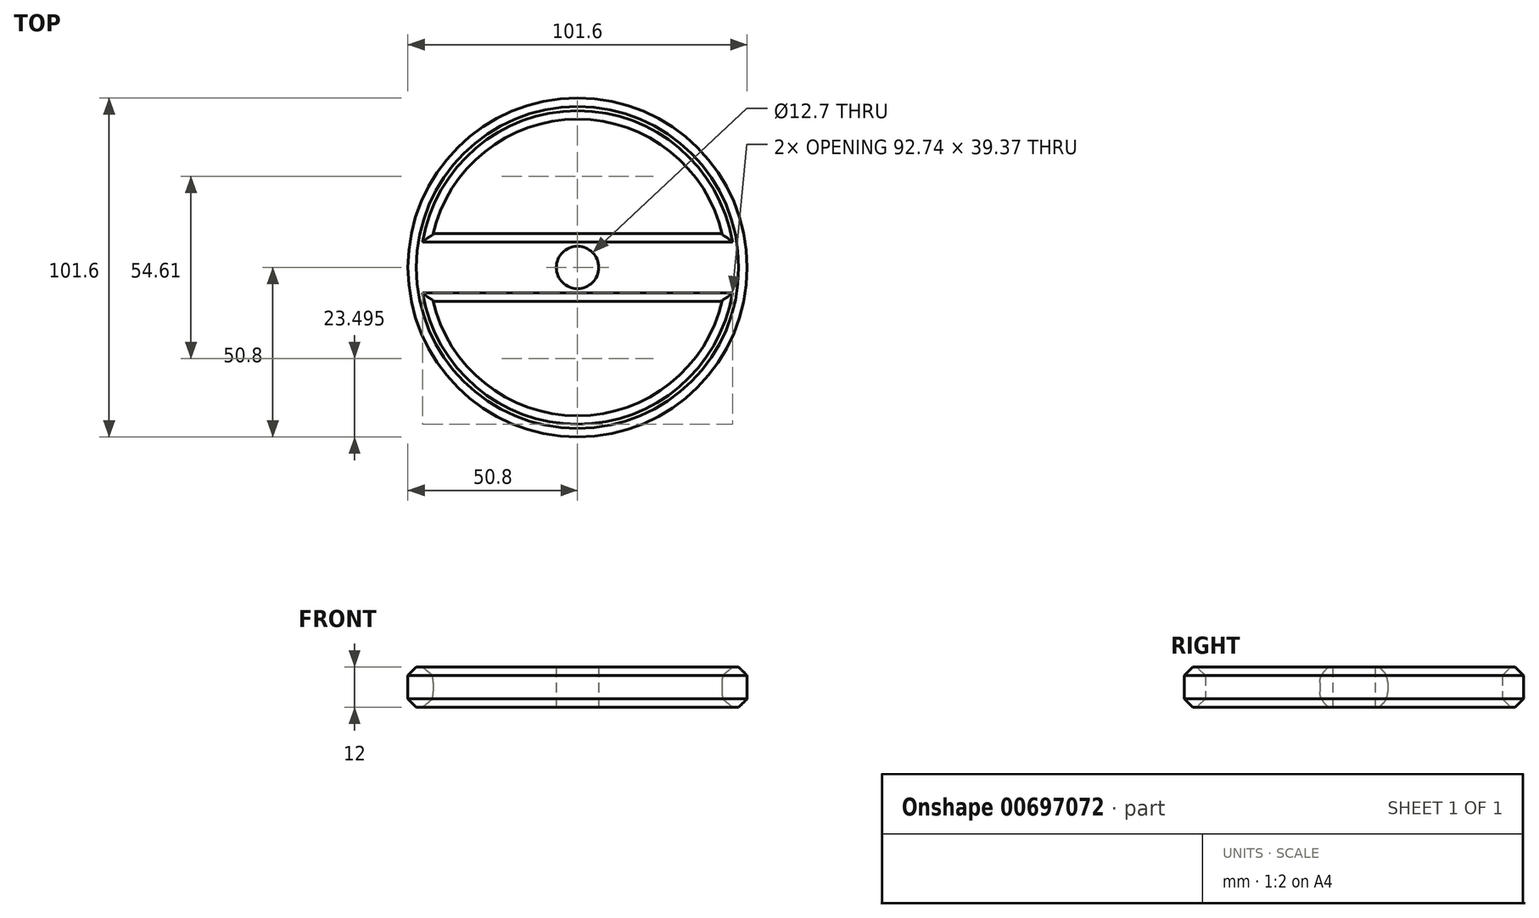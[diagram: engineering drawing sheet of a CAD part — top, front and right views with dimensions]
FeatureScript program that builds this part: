
annotation { "Feature Type Name" : "Feature", "Feature Type Description" : "" }
export const myFeature = defineFeature(function(context is Context, id is Id, definition is map)
    precondition{}
    {
        {
            var Q0;
            Q0=qCreatedBy(makeId("Top.planeOp"),FACE);
            var sketch = newSketch(context, id + "F0", { "sketchPlane" : qUnion([Q0])});
            skCircle(sketch, "E0", {"center": v(0, 0) * mm, "radius": 50.8 * mm});
            skCircle(sketch, "E1", {"center": v(0, 0) * mm, "radius": 44.45 * mm});
            skLineSegment(sketch, "E2.bottom", {"start": v(-43.27, 10.16) * mm, "end": v(43.27, 10.16) * mm});
            skLineSegment(sketch, "E2.top", {"start": v(-43.27, -10.16) * mm, "end": v(43.27, -10.16) * mm});
            skSolve(sketch);
        }
        {
            var Q0;
            Q0=makeQuery(id+"F0.imprint","IMPRINT",FACE,{"disambiguationData":[TD([[makeQuery(id+"F0.imprint","IMPRINT",EDGE,{"derivedFrom":sQuery(id+"F0.wireOp",EDGE,"E0")}),1.0]])]});
            var Q1;
            {var subQ0=sQuery(id+"F0.wireOp",EDGE,"E2.bottom");Q1=makeQuery(id+"F0.imprint","IMPRINT",FACE,{"disambiguationData":[TD([[makeQuery(id+"F0.imprint","IMPRINT",EDGE,{"derivedFrom":subQ0}),-1.0]])]});}
            extrude(context, id + "F1", {"entities" : qUnion([Q0, Q1]), "depth" : 12 * mm, "offsetDistance" : 25.4 * mm});
        }
        {
            var Q0;
            Q0=makeQuery(id+"F1.opExtrude","CAP_EDGE",EDGE,{"disambiguationData":[OSD([sQuery(id+"F0.wireOp",EDGE,"E0")])],"isStart":false});
            var Q1;
            Q1=makeQuery(id+"F1.opExtrude","CAP_EDGE",EDGE,{"disambiguationData":[OSD([sQuery(id+"F0.wireOp",EDGE,"E0")])],"isStart":true});
            var Q2;
            {var subQ0=sQuery(id+"F0.wireOp",EDGE,"E2.top");var subQ1=sQuery(id+"F0.wireOp",EDGE,"E1");Q2=makeQuery(id+"F1.opExtrude","CAP_EDGE",EDGE,{"disambiguationData":[OSD([subQ1]),TDD([makeQuery(id+"F0.imprint","IMPRINT",EDGE,{"disambiguationData":[TD([[makeQuery(id+"F0.imprint","INTERSECT",VERTEX,{"disambiguationData":[OD(0.0)],"derivedFrom":[subQ1,subQ0]}),-1.0]])],"derivedFrom":subQ1})])],"isStart":true});}
            var Q3;
            {var subQ0=sQuery(id+"F0.wireOp",EDGE,"E2.bottom");var subQ1=sQuery(id+"F0.wireOp",EDGE,"E1");Q3=makeQuery(id+"F1.opExtrude","CAP_EDGE",EDGE,{"disambiguationData":[OSD([subQ1]),TDD([makeQuery(id+"F0.imprint","IMPRINT",EDGE,{"disambiguationData":[TD([[makeQuery(id+"F0.imprint","INTERSECT",VERTEX,{"disambiguationData":[OD(0.0)],"derivedFrom":[subQ1,subQ0]}),1.0]])],"derivedFrom":subQ1})])],"isStart":true});}
            var Q4;
            {var subQ0=sQuery(id+"F0.wireOp",EDGE,"E2.top");var subQ1=sQuery(id+"F0.wireOp",EDGE,"E1");Q4=makeQuery(id+"F1.opExtrude","CAP_EDGE",EDGE,{"disambiguationData":[OSD([subQ1]),TDD([makeQuery(id+"F0.imprint","IMPRINT",EDGE,{"disambiguationData":[TD([[makeQuery(id+"F0.imprint","INTERSECT",VERTEX,{"disambiguationData":[OD(0.0)],"derivedFrom":[subQ1,subQ0]}),-1.0]])],"derivedFrom":subQ1})])],"isStart":false});}
            var Q5;
            {var subQ0=sQuery(id+"F0.wireOp",EDGE,"E2.bottom");var subQ1=sQuery(id+"F0.wireOp",EDGE,"E1");Q5=makeQuery(id+"F1.opExtrude","CAP_EDGE",EDGE,{"disambiguationData":[OSD([subQ1]),TDD([makeQuery(id+"F0.imprint","IMPRINT",EDGE,{"disambiguationData":[TD([[makeQuery(id+"F0.imprint","INTERSECT",VERTEX,{"disambiguationData":[OD(0.0)],"derivedFrom":[subQ1,subQ0]}),1.0]])],"derivedFrom":subQ1})])],"isStart":false});}
            chamfer(context, id + "F2", {"entities" : qUnion([Q0, Q1, Q2, Q3, Q4, Q5]), "width" : 2.54 * mm, "tangentPropagation" : true});
        }
        {
            var Q0;
            Q0=makeQuery(id+"F1.opExtrude","CAP_EDGE",EDGE,{"disambiguationData":[OSD([sQuery(id+"F0.wireOp",EDGE,"E2.top")])],"isStart":true});
            var Q1;
            Q1=makeQuery(id+"F1.opExtrude","CAP_EDGE",EDGE,{"disambiguationData":[OSD([sQuery(id+"F0.wireOp",EDGE,"E2.bottom")])],"isStart":true});
            var Q2;
            Q2=makeQuery(id+"F1.opExtrude","CAP_EDGE",EDGE,{"disambiguationData":[OSD([sQuery(id+"F0.wireOp",EDGE,"E2.bottom")])],"isStart":false});
            var Q3;
            Q3=makeQuery(id+"F1.opExtrude","CAP_EDGE",EDGE,{"disambiguationData":[OSD([sQuery(id+"F0.wireOp",EDGE,"E2.top")])],"isStart":false});
            chamfer(context, id + "F3", {"entities" : qUnion([Q0, Q1, Q2, Q3]), "width" : 2.54 * mm, "tangentPropagation" : true});
        }
        {
            var Q0;
            {var subQ0=sQuery(id+"F0.wireOp",EDGE,"E2.bottom");Q0=makeQuery(id+"F3.opChamfer","BLEND_EDGE",EDGE,{"blendedFrom":[makeQuery(id+"F1.opExtrude","CAP_EDGE",EDGE,{"disambiguationData":[OSD([subQ0])],"isStart":true}),makeQuery(id+"F1.opExtrude","SWEPT_FACE",FACE,{"disambiguationData":[OSD([subQ0])]})],"blendedInto":[makeQuery(id+"F1.opExtrude","SWEPT_FACE",FACE,{"disambiguationData":[OSD([subQ0])]})]});}
            var Q1;
            {var subQ0=sQuery(id+"F0.wireOp",EDGE,"E2.bottom");Q1=makeQuery(id+"F3.opChamfer","BLEND_EDGE",EDGE,{"blendedFrom":[makeQuery(id+"F1.opExtrude","CAP_EDGE",EDGE,{"disambiguationData":[OSD([subQ0])],"isStart":false}),makeQuery(id+"F1.opExtrude","SWEPT_FACE",FACE,{"disambiguationData":[OSD([subQ0])]})],"blendedInto":[makeQuery(id+"F1.opExtrude","SWEPT_FACE",FACE,{"disambiguationData":[OSD([subQ0])]})]});}
            var Q2;
            {var subQ0=sQuery(id+"F0.wireOp",EDGE,"E2.top");Q2=makeQuery(id+"F3.opChamfer","BLEND_EDGE",EDGE,{"blendedFrom":[makeQuery(id+"F1.opExtrude","CAP_EDGE",EDGE,{"disambiguationData":[OSD([subQ0])],"isStart":false}),makeQuery(id+"F1.opExtrude","SWEPT_FACE",FACE,{"disambiguationData":[OSD([subQ0])]})],"blendedInto":[makeQuery(id+"F1.opExtrude","SWEPT_FACE",FACE,{"disambiguationData":[OSD([subQ0])]})]});}
            var Q3;
            {var subQ0=sQuery(id+"F0.wireOp",EDGE,"E2.top");Q3=makeQuery(id+"F3.opChamfer","BLEND_EDGE",EDGE,{"blendedFrom":[makeQuery(id+"F1.opExtrude","CAP_EDGE",EDGE,{"disambiguationData":[OSD([subQ0])],"isStart":true}),makeQuery(id+"F1.opExtrude","SWEPT_FACE",FACE,{"disambiguationData":[OSD([subQ0])]})],"blendedInto":[makeQuery(id+"F1.opExtrude","SWEPT_FACE",FACE,{"disambiguationData":[OSD([subQ0])]})]});}
            fillet(context, id + "F4", {"entities" : qUnion([Q0, Q1, Q2, Q3]), "radius" : 5.08 * mm, "tangentPropagation" : true, "allowEdgeOverflow" : false});
        }
        {
            var Q0;
            Q0=qCreatedBy(makeId("Top.planeOp"),FACE);
            var sketch = newSketch(context, id + "F5", { "sketchPlane" : qUnion([Q0])});
            skCircle(sketch, "E3", {"center": v(0, 0) * mm, "radius": 6.35 * mm});
            skSolve(sketch);
        }
        {
            var Q0;
            Q0=sQuery(id+"F5.wireOp",VERTEX,"E3.center");
            var Q1;
            Q1=makeQuery(id+"F1.opExtrude","SWEPT_BODY",BODY,{"disambiguationData":[OSD([sQuery(id+"F0.wireOp",EDGE,"E0"),sQuery(id+"F0.wireOp",EDGE,"E1"),sQuery(id+"F0.wireOp",EDGE,"E2.bottom"),sQuery(id+"F0.wireOp",EDGE,"E2.top")])]});
            hole(context, id + "F6", {"style" : HoleStyle.SIMPLE, "endStyle" : HoleEndStyle.THROUGH, "oppositeDirection" : true, "holeDiameter" : 12.7 * mm, "majorDiameter" : 6.35 * mm, "isTappedThrough" : true, "tappedDepth" : 12.7 * mm, "tapClearance" : 3, "startFromSketch" : true, "locations" : qUnion([Q0]), "scope" : qUnion([Q1])});
        }
    });
